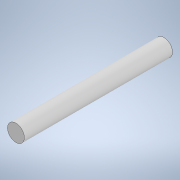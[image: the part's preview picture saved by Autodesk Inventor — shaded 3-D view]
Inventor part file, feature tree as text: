
AUTODESK INVENTOR PART (.ipt)
format: ipt  version: 2022 (Build 260153000, 153)  size: 95,232 bytes
history: native  units: mm
features: other x2, plane x1, extrude x1, sketch x1, reference x1
ambient origin geometry x8: Origin, YZ Plane, XZ Plane, XY Plane, X Axis, Y Axis, Z Axis, Center Point
bodies: Solid1 (feature_tree)
feature tree (6):
  plane  "Work Plane1"
  extrude  "Extrusion1"  [1 undecoded]
  sketch  "Sketch1"  dims[d0=11.0mm d1=0.0mm]
  reference  "Reference1"
  other  "Caja_Reductora_.iam"
  other  "Eje_Salida:1"
note: 1 required parameter value undecoded (feature->parameter linkage not recoverable at this tier; creation-order binding heuristic only, values carry confidence <= 0.55)
